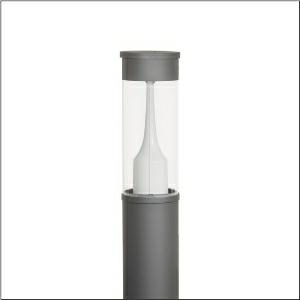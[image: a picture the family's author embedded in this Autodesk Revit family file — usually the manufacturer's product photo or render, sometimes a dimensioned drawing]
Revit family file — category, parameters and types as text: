
# Revit family: city-light_260_iq___p1_0a_5xa5295lf14h_3d8e
name_source: partatom
category: Lighting Fixtures
units: mm (PartAtom-declared; Revit-internal decimal feet)

## family parameters
Cut with Voids When Loaded = No
Host = Face
Light Source = No
Part Type = Normal
Room Calculation Point = No
Round Connector Dimension = Use Diameter
Shared = No

## types (1)
- --- (1 x LED, 1510 lm, 10 W, 4000K)
    Apparent Load = 10 VA
    CIE Flux Codes = 32 61 90 93 100
    Color Rendering = 70
    Color Temperature = 4000K
    Default Elevation = 1800 mm
    Description = City-Light 260 iQ, light pillar, Module 540 iQ-SR, primary light control with 3 zone facetted reflector, of plastic, silver coated, highly specular, structured, primary optical cover: cover, of PMMA, transparent, partly coated, light distribution: P1.0a, primary light characteristic: strongly asymmetric, LED, High Power LED, rated luminous flux: 1.510lm, luminous efficacy: 151lm/W, light colour: 740, colour temperature: 4000K, control gear: ECG iQ, control: presetting dimming logarithmic, Street-Remote, Auto-Match, Temp-Guard, Lumen-Switch, Night-Set, Smart-Wire, Light-Fading, Desk-Remote (wireless, voltage-free reading and setting of iQ features in the workshop via application-optimized NFC function/RFID function), optimised constant luminous flux control (CLO 2.0), with terminal, 6-pole, max. 2.5mm², mains connection: 220..240V, AC, 50/60Hz, start of lifetime: 10W, end of lifetime: 10W, reduction: 5W, luminaire housing, cylindrical, of extruded aluminium section, coated, Siteco® metallic grey (DB 702S), length: 2.600mm, diameter: 200mm, Module 540 iQ-SR, traffic white (RAL 9016), equipment: standard, protection rating (complete): IP65, insulation class (complete): insulation class II (safety insulation), certification: CE, ENEC, VDE, packaging unit: 1 piece

Light Distribution: P1.0a
    Height = 500 mm
    Lamp = 1 x LED
    Lamp Light Flux = 1510 lm
    Lamp Power = 10 W
    Lamp count = 1
    Length = 200 mm  [stored 0.656168 ft]
    Luminous efficacy = 151 lm/W
    Manufacturer = Siteco
    ModVariant = No
    Model = 5XA5295LF14H
    Number of Poles = 1
    OnlyDefault = Yes
    Power Factor = 1
    Product Name = City-Light 260 iQ | P1.0a
    Product group = light pillar | pylon top
    ProductGroupID = 6103
    Protection Class = Protection class II
    Protection Degree = IP 65
    RLX_Detail_Level = 1
    RlxData = <blob elided: 56801 chars, md5=b4c57b4d>
    Socket = socket
    Standby Power = 0 W
    System Light Flux = 1510 lm
    System Power = 10 W
    Type Comments = factory setting: luminous flux: 100 % | dim-lin: 254 | 401 mA
    Type Image = l_1006918.jpg
    URL = http://relux.com
    VarID = @adj_070711
    Voltage = 0 V
    Weight = 0.00 kg
    Width = 0 mm  [stored 0 ft]

note: [stored X ft] marks values corroborated as IEEE doubles in the binary element streams (Revit-internal decimal feet)

## geometry (parser evidence)
native form markers: Blend x4, Sweep x12
no freeform markers — native parametric forms only
